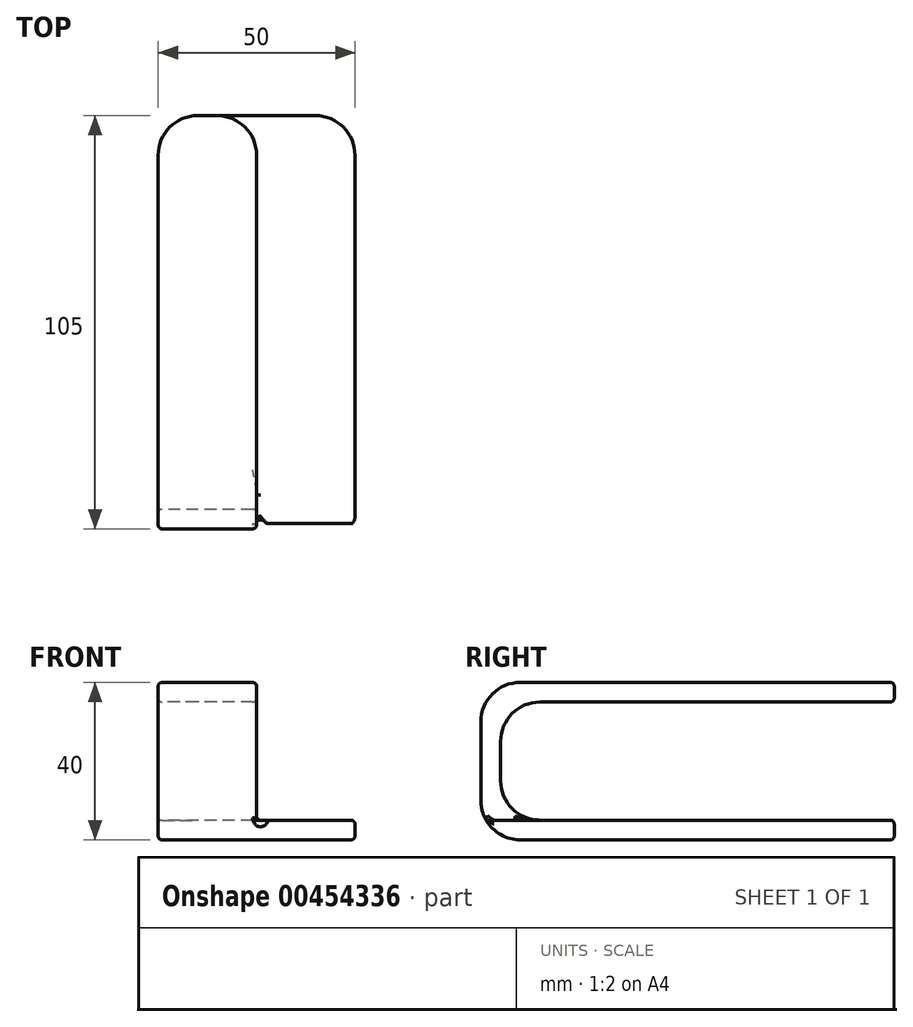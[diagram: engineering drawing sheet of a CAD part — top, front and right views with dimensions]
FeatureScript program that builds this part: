
annotation { "Feature Type Name" : "Feature", "Feature Type Description" : "" }
export const myFeature = defineFeature(function(context is Context, id is Id, definition is map)
    precondition{}
    {
        {
            var Q0;
            Q0=qCreatedBy(makeId("Right.planeOp"),FACE);
            var sketch = newSketch(context, id + "F0", { "sketchPlane" : qUnion([Q0])});
            skLineSegment(sketch, "E0", {"start": v(-18.58, -10.36) * mm, "end": v(-18.58, 19.64) * mm});
            skLineSegment(sketch, "E1", {"start": v(-18.58, 19.64) * mm, "end": v(81.42, 19.64) * mm});
            skLineSegment(sketch, "E2", {"start": v(81.42, 19.64) * mm, "end": v(81.42, 24.64) * mm});
            skLineSegment(sketch, "E3", {"start": v(81.42, 24.64) * mm, "end": v(-23.58, 24.64) * mm});
            skLineSegment(sketch, "E4", {"start": v(-23.58, 24.64) * mm, "end": v(-23.58, -15.36) * mm});
            skLineSegment(sketch, "E5", {"start": v(-23.58, -15.36) * mm, "end": v(81.42, -15.36) * mm});
            skLineSegment(sketch, "E6", {"start": v(81.42, -15.36) * mm, "end": v(81.42, -10.36) * mm});
            skLineSegment(sketch, "E7", {"start": v(81.42, -10.36) * mm, "end": v(-18.58, -10.36) * mm});
            skSolve(sketch);
        }
        {
            var Q0;
            Q0=qSketchRegion(id+"F0",true);
            extrude(context, id + "F1", {"entities" : qUnion([Q0]), "depth" : 25 * mm});
        }
        {
            var Q0;
            Q0=makeQuery(id+"F1.opExtrude","CAP_FACE",FACE,{"disambiguationData":[OSD([sQuery(id+"F0.wireOp",EDGE,"E0"),sQuery(id+"F0.wireOp",EDGE,"E1"),sQuery(id+"F0.wireOp",EDGE,"E2"),sQuery(id+"F0.wireOp",EDGE,"E3"),sQuery(id+"F0.wireOp",EDGE,"E4"),sQuery(id+"F0.wireOp",EDGE,"E5"),sQuery(id+"F0.wireOp",EDGE,"E6"),sQuery(id+"F0.wireOp",EDGE,"E7")])],"isStart":false});
            var sketch = newSketch(context, id + "F2", { "sketchPlane" : qUnion([Q0])});
            skPoint(sketch, "E8.0", {"position": v(81.42, -10.36) * mm});
            skPoint(sketch, "E9.0", {"position": v(-23.58, -15.36) * mm});
            skLineSegment(sketch, "E10.bottom", {"start": v(81.42, -10.36) * mm, "end": v(-23.58, -10.36) * mm});
            skLineSegment(sketch, "E10.top", {"start": v(81.42, -15.36) * mm, "end": v(-23.58, -15.36) * mm});
            skLineSegment(sketch, "E10.left", {"start": v(81.42, -10.36) * mm, "end": v(81.42, -15.36) * mm});
            skLineSegment(sketch, "E10.right", {"start": v(-23.58, -10.36) * mm, "end": v(-23.58, -15.36) * mm});
            skSolve(sketch);
        }
        {
            var Q0;
            Q0=qSketchRegion(id+"F2",true);
            extrude(context, id + "F3", {"entities" : qUnion([Q0]), "operationType" : NewBodyOperationType.ADD, "depth" : 25 * mm});
        }
        {
            var Q0;
            Q0=makeQuery(id+"F1.opExtrude","SWEPT_EDGE",EDGE,{"disambiguationData":[OSD([sQuery(id+"F0.wireOp",EDGE,"E3"),sQuery(id+"F0.wireOp",EDGE,"E4")])]});
            var Q1;
            Q1=makeQuery(id+"F3.boolean.opBoolean","MERGE",EDGE,{"derivedFrom":[makeQuery(id+"F1.opExtrude","SWEPT_EDGE",EDGE,{"disambiguationData":[OSD([sQuery(id+"F0.wireOp",EDGE,"E4"),sQuery(id+"F0.wireOp",EDGE,"E5")])]}),makeQuery(id+"F3.opExtrude","SWEPT_EDGE",EDGE,{"disambiguationData":[OSD([sQuery(id+"F2.wireOp",EDGE,"E10.top"),sQuery(id+"F2.wireOp",EDGE,"E10.right")])]})]});
            var Q2;
            Q2=makeQuery(id+"F1.opExtrude","SWEPT_EDGE",EDGE,{"disambiguationData":[OSD([sQuery(id+"F0.wireOp",EDGE,"E0"),sQuery(id+"F0.wireOp",EDGE,"E7")])]});
            var Q3;
            Q3=makeQuery(id+"F1.opExtrude","SWEPT_EDGE",EDGE,{"disambiguationData":[OSD([sQuery(id+"F0.wireOp",EDGE,"E0"),sQuery(id+"F0.wireOp",EDGE,"E1")])]});
            var Q4;
            Q4=makeQuery(id+"F1.opExtrude","CAP_EDGE",EDGE,{"disambiguationData":[OSD([sQuery(id+"F0.wireOp",EDGE,"E2")])],"isStart":true});
            var Q5;
            Q5=makeQuery(id+"F1.opExtrude","CAP_EDGE",EDGE,{"disambiguationData":[OSD([sQuery(id+"F0.wireOp",EDGE,"E2")])],"isStart":false});
            var Q6;
            Q6=makeQuery(id+"F1.opExtrude","CAP_EDGE",EDGE,{"disambiguationData":[OSD([sQuery(id+"F0.wireOp",EDGE,"E6")])],"isStart":true});
            var Q7;
            Q7=makeQuery(id+"F3.opExtrude","CAP_EDGE",EDGE,{"disambiguationData":[OSD([sQuery(id+"F2.wireOp",EDGE,"E10.left")])],"isStart":false});
            fillet(context, id + "F4", {"entities" : qUnion([Q0, Q1, Q2, Q3, Q4, Q5, Q6, Q7]), "radius" : 10 * mm, "tangentPropagation" : true, "allowEdgeOverflow" : false});
        }
        {
            var Q0;
            Q0=makeQuery(id+"F1.opExtrude","CAP_FACE",FACE,{"disambiguationData":[OSD([sQuery(id+"F0.wireOp",EDGE,"E0"),sQuery(id+"F0.wireOp",EDGE,"E1"),sQuery(id+"F0.wireOp",EDGE,"E2"),sQuery(id+"F0.wireOp",EDGE,"E3"),sQuery(id+"F0.wireOp",EDGE,"E4"),sQuery(id+"F0.wireOp",EDGE,"E5"),sQuery(id+"F0.wireOp",EDGE,"E6"),sQuery(id+"F0.wireOp",EDGE,"E7")])],"isStart":false});
            var Q1;
            Q1=makeQuery(id+"FbNcf2MhP7G3Cr6_1.boolean.opBoolean","MERGE",FACE,{"derivedFrom":[makeQuery(id+"F1.opExtrude","CAP_FACE",FACE,{"disambiguationData":[OSD([sQuery(id+"F0.wireOp",EDGE,"E0"),sQuery(id+"F0.wireOp",EDGE,"E1"),sQuery(id+"F0.wireOp",EDGE,"E2"),sQuery(id+"F0.wireOp",EDGE,"E3"),sQuery(id+"F0.wireOp",EDGE,"E4"),sQuery(id+"F0.wireOp",EDGE,"E5"),sQuery(id+"F0.wireOp",EDGE,"E6"),sQuery(id+"F0.wireOp",EDGE,"E7")])],"isStart":true}),makeQuery(id+"FbNcf2MhP7G3Cr6_1.opExtrude","SWEPT_FACE",FACE,{"disambiguationData":[OSD([sQuery(id+"FPQwV7vsUhrATf5_1.wireOp",EDGE,"80395d0b-2d0b-45fb-b214-da32a1259ecb.0.0")])]})]});
            fillet(context, id + "F5", {"entities" : qUnion([Q0, Q1]), "radius" : 1 * mm, "tangentPropagation" : true, "allowEdgeOverflow" : false});
        }
    });
